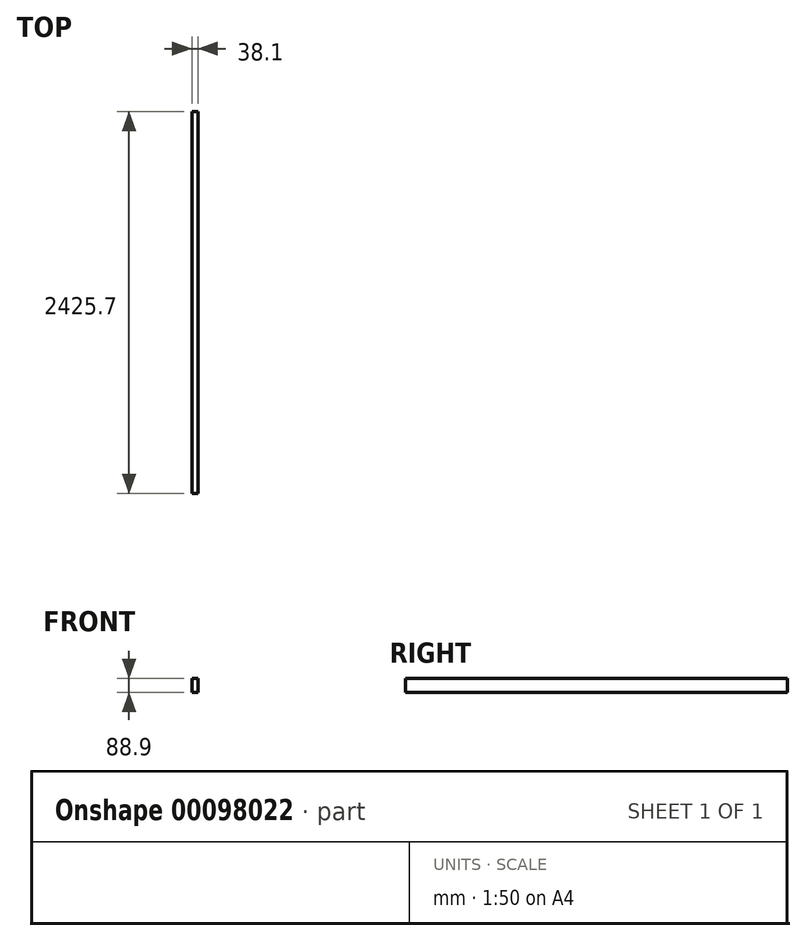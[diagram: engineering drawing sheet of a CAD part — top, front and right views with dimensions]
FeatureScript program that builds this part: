
annotation { "Feature Type Name" : "Feature", "Feature Type Description" : "" }
export const myFeature = defineFeature(function(context is Context, id is Id, definition is map)
    precondition{}
    {
        {
            var Q0;
            Q0=qCreatedBy(makeId("Right.planeOp"),FACE);
            var sketch = newSketch(context, id + "F0", { "sketchPlane" : qUnion([Q0])});
            skLineSegment(sketch, "E0.bottom", {"start": v(1212.85, 44.45) * mm, "end": v(-1212.85, 44.45) * mm});
            skLineSegment(sketch, "E0.top", {"start": v(1212.85, -44.45) * mm, "end": v(-1212.85, -44.45) * mm});
            skLineSegment(sketch, "E0.left", {"start": v(1212.85, 44.45) * mm, "end": v(1212.85, -44.45) * mm});
            skLineSegment(sketch, "E0.right", {"start": v(-1212.85, 44.45) * mm, "end": v(-1212.85, -44.45) * mm});
            skPoint(sketch, "E0.middle", {"position": v(0, 0) * mm});
            skSolve(sketch);
        }
        {
            var Q0;
            Q0=makeQuery(id+"F0.imprint","IMPRINT",FACE,{"disambiguationData":[TD([[makeQuery(id+"F0.imprint","IMPRINT",EDGE,{"derivedFrom":sQuery(id+"F0.wireOp",EDGE,"E0.bottom")}),1.0]])]});
            extrude(context, id + "F1", {"entities" : qUnion([Q0]), "depth" : 38.1 * mm});
        }
    });
